# Revit family: 3-754-15 Pavo Wall Lantern
name_source: partatom
category: Luminarias
units: mm (PartAtom-declared; Revit-internal decimal feet)

## family parameters
Anfitrión = Muro
Compartido = No
Corte con vacíos al cargar = No
Cota de conector redondo = Diámetro de uso
Número OmniClass = 23.80.70.00
Origen de luz = Sí
Punto de cálculo de habitación = No
Siempre vertical = Sí
Tipo de pieza = Normal
Título OmniClass = Lighting

## types (1)
- 3-754-15 / Black - White Frost Glass
    Cambio de temperatura de color de luz atenuada = <Ninguno>
    Elevación por defecto = 0 "
    Fabricante = Oxygen - Lighting & Fans
    Filtro de color = 16777215
    Main Diffuser = White Frost Glass
    Metal Finish = 15 - Black
    Modelo = 3-754-15 Pavo Wall Lantern
    References = Ref. 3 = 120 V / Ref. 37 = 277 V
    Tamaño de símbolo de origen de luz = 24 "
    URL = www.oxygenlighting.com
    Voltage = 120 V
    Voltage Input = 120 V or 277 V - 50/60 Hz

## geometry (parser evidence)
native form markers: Blend x2, Sweep x5
no freeform markers — native parametric forms only
